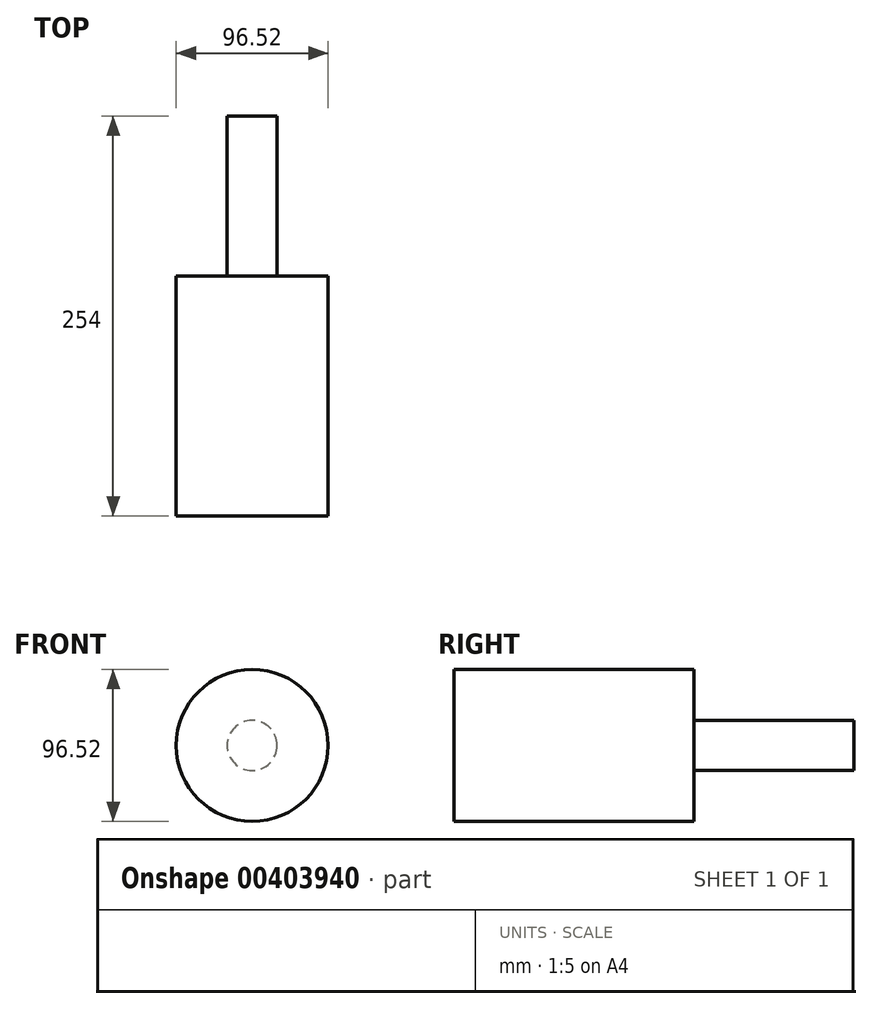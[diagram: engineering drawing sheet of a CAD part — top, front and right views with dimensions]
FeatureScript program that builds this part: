
annotation { "Feature Type Name" : "Feature", "Feature Type Description" : "" }
export const myFeature = defineFeature(function(context is Context, id is Id, definition is map)
    precondition{}
    {
        {
            var Q0;
            Q0=qCreatedBy(makeId("Top.planeOp"),FACE);
            var sketch = newSketch(context, id + "F0", { "sketchPlane" : qUnion([Q0])});
            skLineSegment(sketch, "E0.bottom", {"start": v(0, 0) * mm, "end": v(15.87, 0) * mm});
            skLineSegment(sketch, "E0.top", {"start": v(0, 101.6) * mm, "end": v(15.87, 101.6) * mm});
            skLineSegment(sketch, "E0.left", {"start": v(0, 0) * mm, "end": v(0, 101.6) * mm});
            skLineSegment(sketch, "E0.right", {"start": v(15.87, 0) * mm, "end": v(15.87, 101.6) * mm});
            skLineSegment(sketch, "E1.bottom", {"start": v(0, 0) * mm, "end": v(48.26, 0) * mm});
            skLineSegment(sketch, "E1.top", {"start": v(0, -152.4) * mm, "end": v(48.26, -152.4) * mm});
            skLineSegment(sketch, "E1.left", {"start": v(0, 0) * mm, "end": v(0, -152.4) * mm});
            skLineSegment(sketch, "E1.right", {"start": v(48.26, 0) * mm, "end": v(48.26, -152.4) * mm});
            skSolve(sketch);
        }
        {
            var Q0;
            Q0 = qSketchRegion(id + "F0", true);
            var Q1;
            Q1=sQuery(id+"F0.wireOp",EDGE,"E1.left");
            revolve(context, id + "F1", {"entities" : qUnion([Q0]), "axis" : qUnion([Q1]), "revolveType" : RevolveType.FULL});
        }
    });
